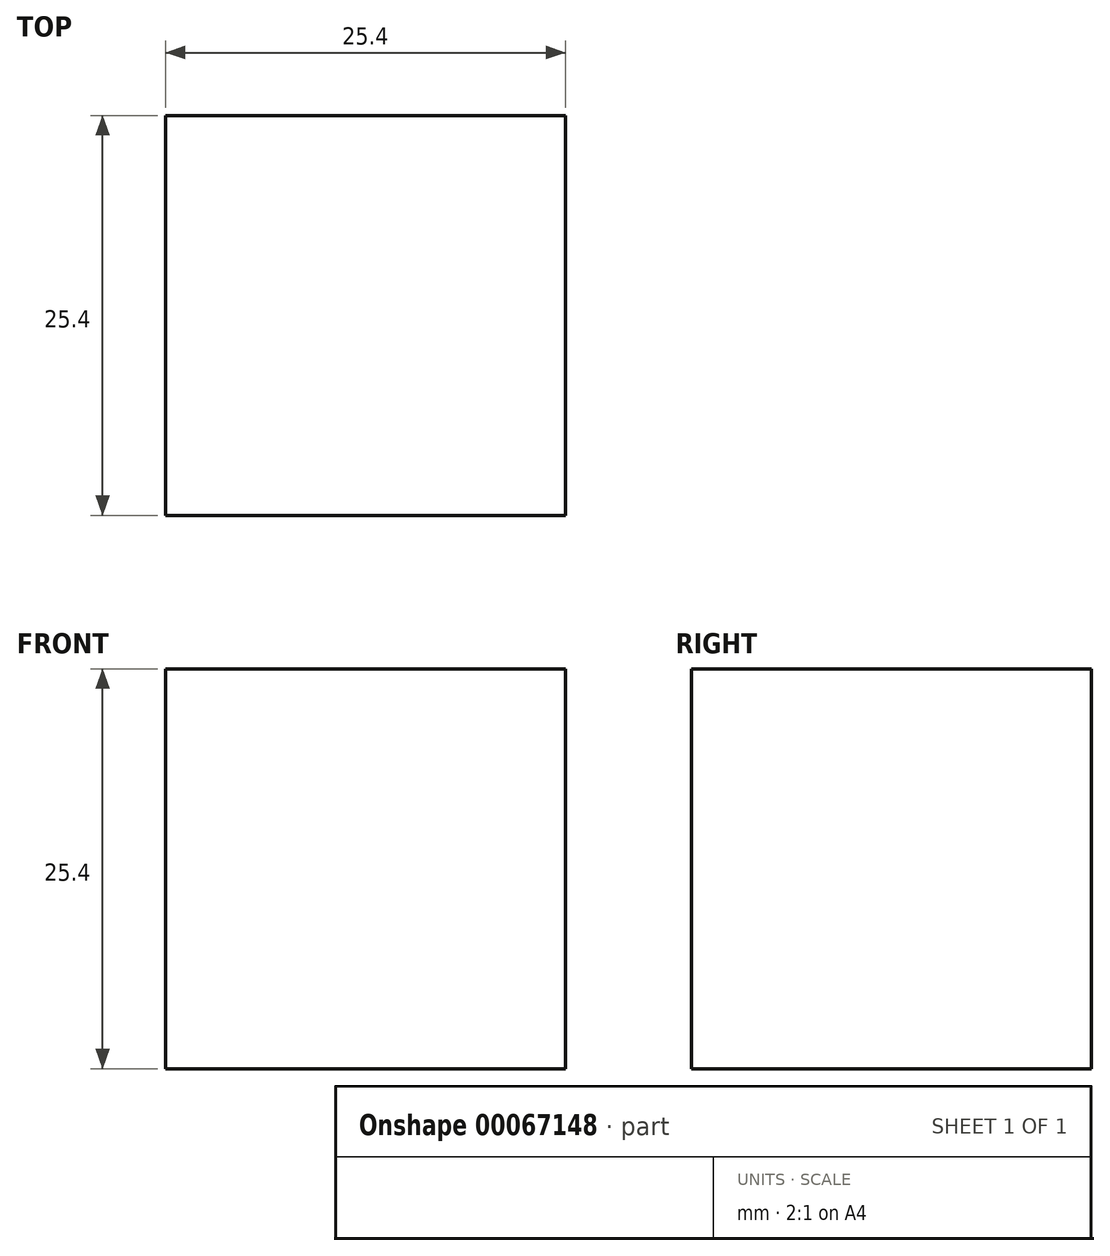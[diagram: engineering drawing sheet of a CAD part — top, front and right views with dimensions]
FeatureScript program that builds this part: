
annotation { "Feature Type Name" : "Feature", "Feature Type Description" : "" }
export const myFeature = defineFeature(function(context is Context, id is Id, definition is map)
    precondition{}
    {
        {
            var Q0;
            Q0=qCreatedBy(makeId("Top.planeOp"),FACE);
            var sketch = newSketch(context, id + "F0", { "sketchPlane" : qUnion([Q0])});
            skLineSegment(sketch, "E0", {"start": v(0, 0) * mm, "end": v(0, 25.4) * mm});
            skLineSegment(sketch, "E1", {"start": v(0, 25.4) * mm, "end": v(-25.4, 25.4) * mm});
            skLineSegment(sketch, "E2", {"start": v(-25.4, 25.4) * mm, "end": v(-25.4, 0) * mm});
            skLineSegment(sketch, "E3", {"start": v(-25.4, 0) * mm, "end": v(0, 0) * mm});
            skSolve(sketch);
        }
        {
            var Q0;
            Q0=makeQuery(id+"F0.imprint","IMPRINT",FACE,{"disambiguationData":[TD([[makeQuery(id+"F0.imprint","IMPRINT",EDGE,{"derivedFrom":sQuery(id+"F0.wireOp",EDGE,"E0")}),1.0]])]});
            extrude(context, id + "F1", {"entities" : qUnion([Q0]), "depth" : 25.4 * mm});
        }
    });
